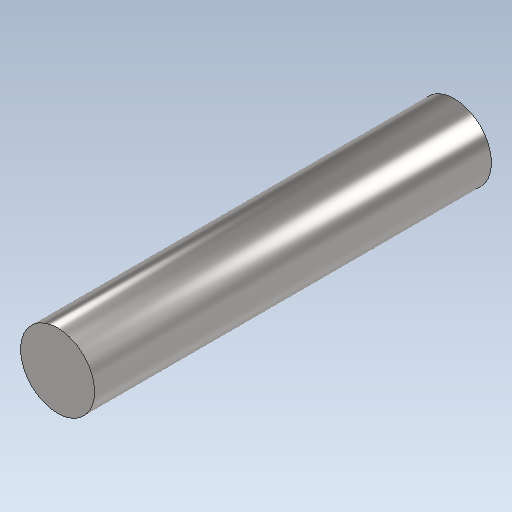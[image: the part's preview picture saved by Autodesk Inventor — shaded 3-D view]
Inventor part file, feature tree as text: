
AUTODESK INVENTOR PART (.ipt)
format: ipt  version: 2023 (Build 270158000, 158)  size: 120,832 bytes
history: native  units: in
note: dims shown in document units (in); Inventor stores cm internally (conversion verified against a paired STEP export)
features: extrude x1, sketch x1
ambient origin geometry x8: Origin, YZ Plane, XZ Plane, XY Plane, X Axis, Y Axis, Z Axis, Center Point
bodies: Solid1 (feature_tree)
feature tree (2):
  extrude  "Extrusion1"  Depth=1.3386in TaperAngle=0.0deg
  sketch  "Sketch1"  dims[d0=0.25in d1=1.3386in d2=0.0in]
